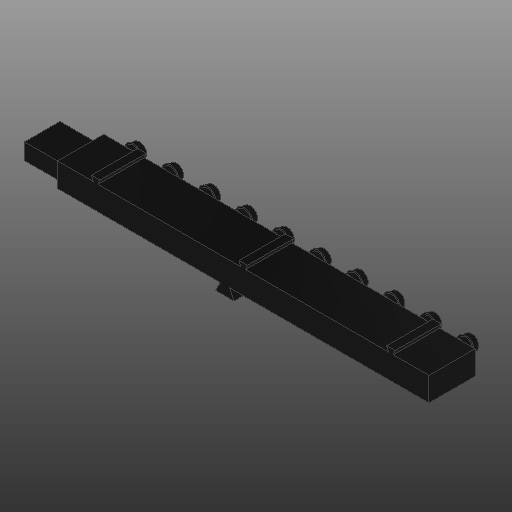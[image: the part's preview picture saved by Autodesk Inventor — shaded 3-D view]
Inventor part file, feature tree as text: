
AUTODESK INVENTOR PART (.ipt)
format: ipt  version: 2020 (Build 240168000, 168)  size: 442,368 bytes
history: native  units: in
note: dims shown in document units (in); Inventor stores cm internally (conversion verified against a paired STEP export)
features: other x8, extrude x5, pattern_linear x2, loft x1, projected_geometry x1, sketch x1
ambient origin geometry x8: Origin, YZ Plane, XZ Plane, XY Plane, X Axis, Y Axis, Z Axis, Center Point
bodies: Solid1 (feature_tree)
feature tree (18):
  other  "CrossSection1"
  other  "Box Sketch"
  extrude  "Box"  Depth=0.5906in
  other  "Fitting Plane"
  other  "Fitting"
  loft  "Fitting Entrance Loft"
  pattern_linear  "Channel Repetition"  Spacing1=0.0in  [1 undecoded]
  extrude  "Small Tabs"  Depth=0.5906in
  extrude  "Big Tabs"  Depth=0.5906in
  extrude  "Connector"  Depth=0.5906in
  pattern_linear  "Connector Fitting Entrance"  Spacing1=0.0492in  [1 undecoded]
  extrude  "End Cap"  Depth=0.5906in
  other  "Fitting Sketch"
  other  "Fitting Entrance Loft From"
  projected_geometry  "Projected Loop1"
  other  "Tab Sketch"
  other  "Fitting Entrance Loft To"
  sketch  "Sketch8"  dims[d0=0.1181in d2=0.0787in d3=0.0787in d7=0.0in d8=0.251in d10=0.0787in d11=0.0197in d12=0.0492in d13=0.0315in d14=0.0938in d15=0.1528in d16=90.0deg d31=0.5906in d32=0.0in d33=0.4872in d34=0.107in d35=0.0619in d36=0.0591in d37=0.107in d38=0.0619in d39=0.0591in d40=0.107in d41=0.0619in d42=0.0591in d49=1.8898in d50=1.8898in d77=0.0295in d79=0.3056in d80=0.0079in d81=0.0079in d82=0.0079in d83=0.0787in d84=0.1299in d85=0.0669in d106=0.4724in d107=0.0in d108=0.1481in d109=0.1528in d110=0.251in d111=0.1245in d113=0.0in d114=90.0deg d115=0.0in d116=90.0deg d117=0.0197in d118=0.0787in d119=-0.125in d120=0.7874in d121=0.7874in d123=0.4724in d124=0.0591in d125=0.0in d128=0.2362in d129=0.1181in d130=0.1181in d131=2.1407in d138=0.5906in d139=0.0in d141=0.0492in d142=0.0492in d9=0.0344in d126=0.0197in d127=0.0344in]
note: 2 required parameter values undecoded (feature->parameter linkage not recoverable at this tier; creation-order binding heuristic only, values carry confidence <= 0.55)
